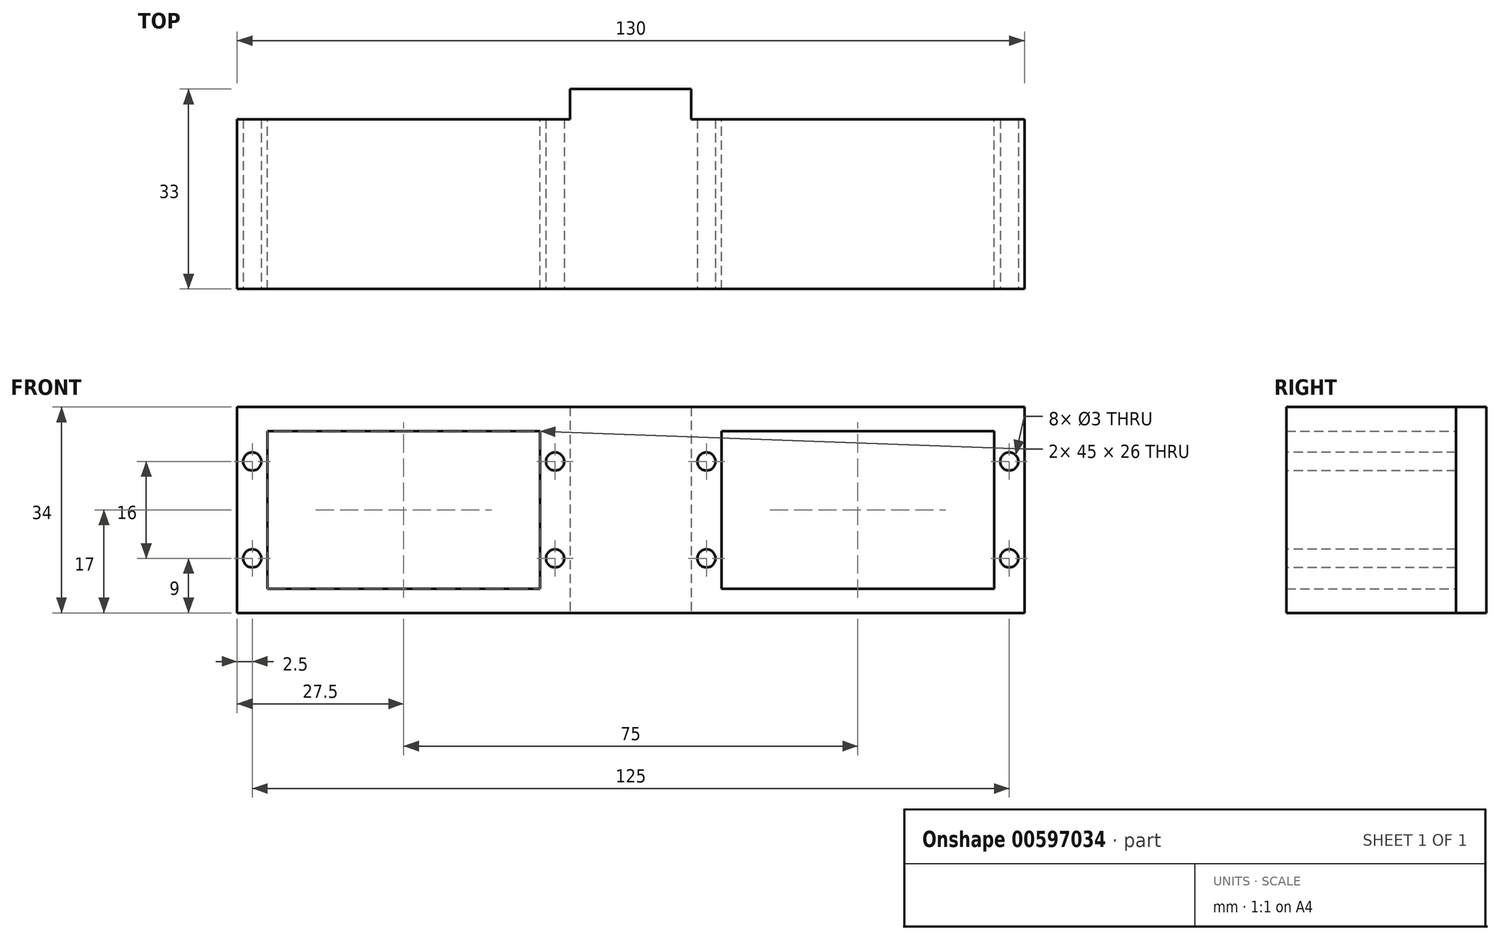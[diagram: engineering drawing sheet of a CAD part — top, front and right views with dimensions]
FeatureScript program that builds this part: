
annotation { "Feature Type Name" : "Feature", "Feature Type Description" : "" }
export const myFeature = defineFeature(function(context is Context, id is Id, definition is map)
    precondition{}
    {
        {
            var Q0;
            Q0=qCreatedBy(makeId("Front.planeOp"),FACE);
            var sketch = newSketch(context, id + "F0", { "sketchPlane" : qUnion([Q0])});
            skLineSegment(sketch, "E0.bottom", {"start": v(27.5, 17) * mm, "end": v(-27.5, 17) * mm});
            skLineSegment(sketch, "E0.top", {"start": v(27.5, -17) * mm, "end": v(-27.5, -17) * mm});
            skLineSegment(sketch, "E0.left", {"start": v(27.5, 17) * mm, "end": v(27.5, -17) * mm});
            skLineSegment(sketch, "E0.right", {"start": v(-27.5, 17) * mm, "end": v(-27.5, -17) * mm});
            skPoint(sketch, "E0.middle", {"position": v(0, 0) * mm});
            skLineSegment(sketch, "E1.bottom", {"start": v(22.5, 13) * mm, "end": v(-22.5, 13) * mm});
            skLineSegment(sketch, "E1.top", {"start": v(22.5, -13) * mm, "end": v(-22.5, -13) * mm});
            skLineSegment(sketch, "E1.left", {"start": v(22.5, 13) * mm, "end": v(22.5, -13) * mm});
            skLineSegment(sketch, "E1.right", {"start": v(-22.5, 13) * mm, "end": v(-22.5, -13) * mm});
            skLineSegment(sketch, "E2.bottom", {"start": v(27.5, 17) * mm, "end": v(47.5, 17) * mm});
            skLineSegment(sketch, "E2.top", {"start": v(27.5, -17) * mm, "end": v(47.5, -17) * mm});
            skLineSegment(sketch, "E2.right", {"start": v(47.5, 17) * mm, "end": v(47.5, -17) * mm});
            skLineSegment(sketch, "E3.bottom", {"start": v(47.5, 17) * mm, "end": v(102.5, 17) * mm});
            skLineSegment(sketch, "E3.top", {"start": v(47.5, -17) * mm, "end": v(102.5, -17) * mm});
            skLineSegment(sketch, "E3.right", {"start": v(102.5, 17) * mm, "end": v(102.5, -17) * mm});
            skLineSegment(sketch, "E4.bottom", {"start": v(52.5, 13) * mm, "end": v(97.5, 13) * mm});
            skLineSegment(sketch, "E4.top", {"start": v(52.5, -13) * mm, "end": v(97.5, -13) * mm});
            skLineSegment(sketch, "E4.left", {"start": v(52.5, 13) * mm, "end": v(52.5, -13) * mm});
            skLineSegment(sketch, "E4.right", {"start": v(97.5, 13) * mm, "end": v(97.5, -13) * mm});
            skSolve(sketch);
        }
        {
            var Q0;
            Q0 = qSketchRegion(id + "F0", true);
            extrude(context, id + "F1", {"entities" : qUnion([Q0]), "endBound" : BoundingType.SYMMETRIC, "depth" : 28 * mm, "offsetDistance" : 25.4 * mm});
        }
        {
            var Q0;
            Q0=makeQuery(id+"F1.opExtrude","CAP_FACE",FACE,{"disambiguationData":[OSD([sQuery(id+"F0.wireOp",EDGE,"E0.bottom"),sQuery(id+"F0.wireOp",EDGE,"E0.top"),sQuery(id+"F0.wireOp",EDGE,"E0.right"),sQuery(id+"F0.wireOp",EDGE,"E1.bottom"),sQuery(id+"F0.wireOp",EDGE,"E1.top"),sQuery(id+"F0.wireOp",EDGE,"E1.left"),sQuery(id+"F0.wireOp",EDGE,"E1.right"),sQuery(id+"F0.wireOp",EDGE,"E2.bottom"),sQuery(id+"F0.wireOp",EDGE,"E2.top"),sQuery(id+"F0.wireOp",EDGE,"E3.bottom"),sQuery(id+"F0.wireOp",EDGE,"E3.top"),sQuery(id+"F0.wireOp",EDGE,"E3.right"),sQuery(id+"F0.wireOp",EDGE,"E4.bottom"),sQuery(id+"F0.wireOp",EDGE,"E4.top"),sQuery(id+"F0.wireOp",EDGE,"E4.left"),sQuery(id+"F0.wireOp",EDGE,"E4.right")])],"isStart":false});
            var sketch = newSketch(context, id + "F2", { "sketchPlane" : qUnion([Q0])});
            skLineSegment(sketch, "E5", {"start": v(-27.5, 0) * mm, "end": v(102.5, 0) * mm, "construction": true});
            skLineSegment(sketch, "E6", {"start": v(27.5, 17) * mm, "end": v(27.5, -17) * mm, "construction": true});
            skCircle(sketch, "E7", {"center": v(25, 8) * mm, "radius": 1.5 * mm});
            skCircle(sketch, "E8", {"center": v(-25, 8) * mm, "radius": 1.5 * mm});
            skCircle(sketch, "E9.MirrorC", {"center": v(-25, -8) * mm, "radius": 1.5 * mm});
            skCircle(sketch, "E10.MirrorC", {"center": v(25, -8) * mm, "radius": 1.5 * mm});
            skLineSegment(sketch, "E11", {"start": v(37.5, 17) * mm, "end": v(37.5, -17) * mm});
            skCircle(sketch, "E12.MirrorC", {"center": v(50, 8) * mm, "radius": 1.5 * mm});
            skCircle(sketch, "E13.MirrorC", {"center": v(50, -8) * mm, "radius": 1.5 * mm});
            skCircle(sketch, "E14.MirrorC", {"center": v(100, 8) * mm, "radius": 1.5 * mm});
            skCircle(sketch, "E15.MirrorC", {"center": v(100, -8) * mm, "radius": 1.5 * mm});
            skSolve(sketch);
        }
        {
            var Q0;
            Q0 = qSketchRegion(id + "F2", true);
            extrude(context, id + "F3", {"entities" : qUnion([Q0]), "operationType" : NewBodyOperationType.REMOVE, "oppositeDirection" : true, "depth" : 30 * mm, "offsetDistance" : 25.4 * mm});
        }
        {
            var Q0;
            Q0=makeQuery(id+"F1.opExtrude","CAP_FACE",FACE,{"disambiguationData":[OSD([sQuery(id+"F0.wireOp",EDGE,"E0.bottom"),sQuery(id+"F0.wireOp",EDGE,"E0.top"),sQuery(id+"F0.wireOp",EDGE,"E0.right"),sQuery(id+"F0.wireOp",EDGE,"E1.bottom"),sQuery(id+"F0.wireOp",EDGE,"E1.top"),sQuery(id+"F0.wireOp",EDGE,"E1.left"),sQuery(id+"F0.wireOp",EDGE,"E1.right"),sQuery(id+"F0.wireOp",EDGE,"E2.bottom"),sQuery(id+"F0.wireOp",EDGE,"E2.top"),sQuery(id+"F0.wireOp",EDGE,"E3.bottom"),sQuery(id+"F0.wireOp",EDGE,"E3.top"),sQuery(id+"F0.wireOp",EDGE,"E3.right"),sQuery(id+"F0.wireOp",EDGE,"E4.bottom"),sQuery(id+"F0.wireOp",EDGE,"E4.top"),sQuery(id+"F0.wireOp",EDGE,"E4.left"),sQuery(id+"F0.wireOp",EDGE,"E4.right")])],"isStart":true});
            var sketch = newSketch(context, id + "F4", { "sketchPlane" : qUnion([Q0])});
            skLineSegment(sketch, "E16", {"start": v(-37.5, 17) * mm, "end": v(-37.5, -17) * mm, "construction": true});
            skLineSegment(sketch, "E17.bottom", {"start": v(-47.5, 17) * mm, "end": v(-27.5, 17) * mm});
            skLineSegment(sketch, "E17.top", {"start": v(-47.5, -17) * mm, "end": v(-27.5, -17) * mm});
            skLineSegment(sketch, "E17.left", {"start": v(-47.5, 17) * mm, "end": v(-47.5, -17) * mm});
            skLineSegment(sketch, "E17.right", {"start": v(-27.5, 17) * mm, "end": v(-27.5, -17) * mm});
            skSolve(sketch);
        }
        {
            var Q0;
            Q0 = qSketchRegion(id + "F4", true);
            extrude(context, id + "F5", {"entities" : qUnion([Q0]), "operationType" : NewBodyOperationType.ADD, "depth" : 5 * mm, "offsetDistance" : 25.4 * mm});
        }
    });
